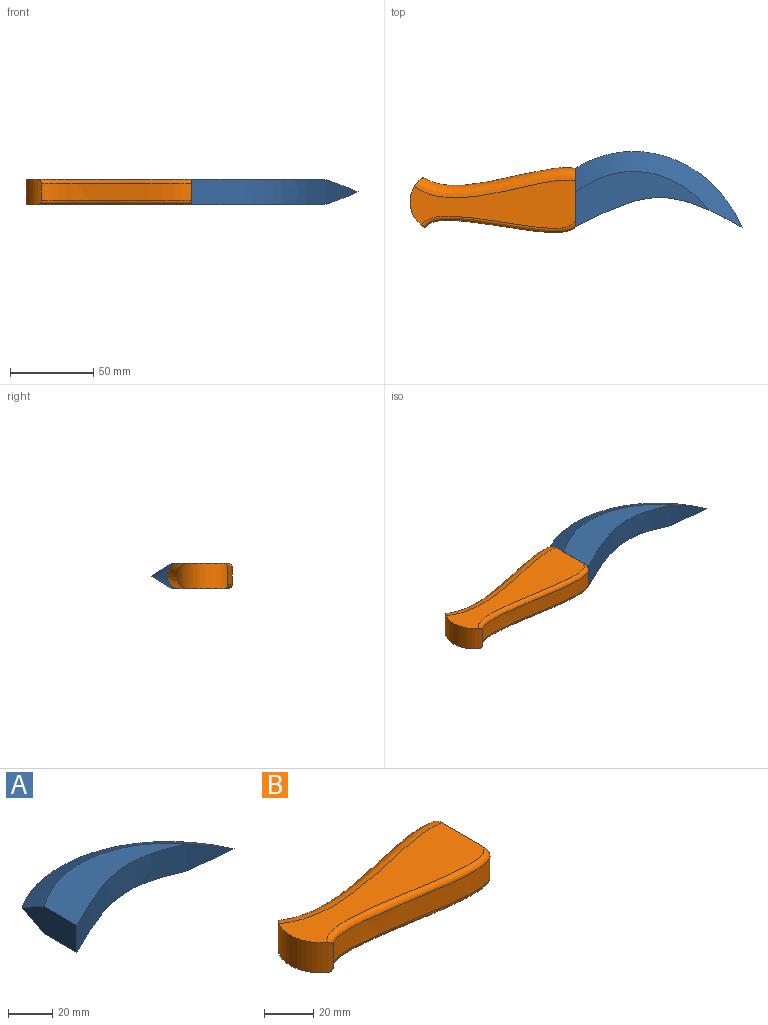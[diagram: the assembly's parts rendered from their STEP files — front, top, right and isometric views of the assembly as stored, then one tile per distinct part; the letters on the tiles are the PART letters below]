
ASSEMBLY  parts=2 mates=1
PART A: 6 faces, bbox 106.7x50.5x15.3 mm
  f0: plane 35.01x15.01mm, normal (-1,0,0), area 419mm2, adj f1,f2,f3,f4,f5
  f1: extruded ~100x17.96mm, area 1432.7mm2, adj f0,f2,f3,f4,f5
  f2: plane 83.09x34.07mm, normal (0,0,1), area 1200.9mm2, adj f0,f1,f5
  f3: plane 83.09x34.06mm, normal (0,0,-1), area 1200.9mm2, adj f0,f1,f4
  f4: bspline ~106.34x50.22mm, area 1487.9mm2, adj f0,f1,f3,f5
  f5: bspline ~106.34x50.22mm, area 1487.4mm2, adj f0,f1,f2,f4
PART B: 9 faces, bbox 104.4x40.1x16.1 mm
  f0: plane 36.11x16.11mm, normal (1,0,0), area 496mm2, adj f2,f3,f4,f5,f6,f7,f8
  f1: cylinder r=17.48mm len=30mm, axis (0,0,-1), area 510.2mm2, adj f2,f3,f4,f5,f6,f7,f8
  f2: extruded ~90x10mm, area 926.2mm2, adj f0,f1,f7,f8
  f3: plane 99.21x28.97mm, normal (0,0,1), area 1871.5mm2, adj f0,f1,f5,f8
  f4: plane 99.21x28.97mm, normal (0,0,-1), area 1871.5mm2, adj f0,f1,f6,f7
  f5: bspline ~99.69x18.19mm, area 1127.4mm2, adj f0,f1,f3,f6
  f6: bspline ~99.69x18.19mm, area 1126.6mm2, adj f0,f1,f4,f5
  f7: bspline ~96.31x10.33mm, area 370.5mm2, adj f0,f1,f2,f4
  f8: bspline ~96.31x10.33mm, area 370.5mm2, adj f0,f1,f2,f3
PLACE A t=(17.52,-46.86,-54.98)mm
PLACE B t=(17.52,-46.86,-54.98)mm
MATE fastened A.f0 <-> B.f0  axis (-1,0,0) through (17.52,-46.42,-54.98)mm
